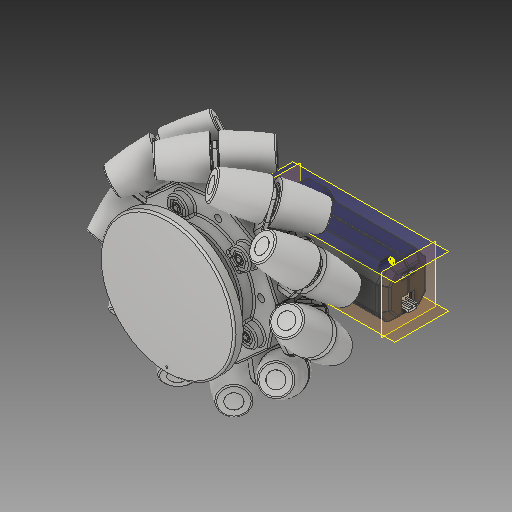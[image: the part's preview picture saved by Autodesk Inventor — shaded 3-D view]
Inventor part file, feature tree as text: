
AUTODESK INVENTOR PART (.ipt)
format: ipt  version: 2019 (Build 230136000, 136)  size: 17,353,216 bytes
history: native  units: in
note: dims shown in document units (in); Inventor stores cm internally (conversion verified against a paired STEP export)
features: other x108, plane x4
ambient origin geometry x8: Origin, YZ Plane, XZ Plane, XY Plane, X Axis, Y Axis, Z Axis, Center Point
bodies: Solid1 (feature_tree)
feature tree (112):
  other  "Wheel Sub-Assembly.iam"
  other  "wheel hubcap.ipt:1"
  other  "6inchMecanumLeft217-2799.20121203.iam:1::217-2799-001 Rev1.ipt:1"
  other  "6inchMecanumLeft217-2799.20121203.iam:1::217-2799-001 Rev1.ipt:2"
  other  "6inchMecanumLeft217-2799.20121203.iam:1::217-2799-002 Rev1.ipt:1"
  other  "6inchMecanumLeft217-2799.20121203.iam:1::217-2586-003 Rev2.ipt:1"
  other  "6inchMecanumLeft217-2799.20121203.iam:1::217-2586-003 Rev2.ipt:2"
  other  "6inchMecanumLeft217-2799.20121203.iam:1::217-2586-004 Rev1.ipt:1"
  other  "6inchMecanumLeft217-2799.20121203.iam:1::217-2586-004 Rev1.ipt:2"
  other  "6inchMecanumLeft217-2799.20121203.iam:1::217-2586-007 Rev1.ipt:1"
  other  "6inchMecanumLeft217-2799.20121203.iam:1::217-2586-008 Rev1.ipt:1"
  other  "6inchMecanumLeft217-2799.20121203.iam:1::NUT-832-NYLOCK.ipt:1"
  other  "6inchMecanumLeft217-2799.20121203.iam:1::SCREW-832-1250.ipt:1"
  other  "6inchMecanumLeft217-2799.20121203.iam:1::217-2586-007 Rev1.ipt:2"
  other  "6inchMecanumLeft217-2799.20121203.iam:1::217-2586-007 Rev1.ipt:3"
  other  "6inchMecanumLeft217-2799.20121203.iam:1::217-2586-007 Rev1.ipt:4"
  other  "6inchMecanumLeft217-2799.20121203.iam:1::217-2586-007 Rev1.ipt:5"
  other  "6inchMecanumLeft217-2799.20121203.iam:1::217-2586-007 Rev1.ipt:6"
  other  "6inchMecanumLeft217-2799.20121203.iam:1::217-2586-007 Rev1.ipt:7"
  other  "6inchMecanumLeft217-2799.20121203.iam:1::217-2586-007 Rev1.ipt:8"
  other  "6inchMecanumLeft217-2799.20121203.iam:1::217-2586-007 Rev1.ipt:9"
  other  "6inchMecanumLeft217-2799.20121203.iam:1::217-2586-007 Rev1.ipt:10"
  other  "6inchMecanumLeft217-2799.20121203.iam:1::217-2586-004 Rev1.ipt:3"
  other  "6inchMecanumLeft217-2799.20121203.iam:1::217-2586-004 Rev1.ipt:4"
  other  "6inchMecanumLeft217-2799.20121203.iam:1::217-2586-004 Rev1.ipt:5"
  other  "6inchMecanumLeft217-2799.20121203.iam:1::217-2586-004 Rev1.ipt:6"
  other  "6inchMecanumLeft217-2799.20121203.iam:1::217-2586-004 Rev1.ipt:7"
  other  "6inchMecanumLeft217-2799.20121203.iam:1::217-2586-004 Rev1.ipt:8"
  other  "6inchMecanumLeft217-2799.20121203.iam:1::217-2586-004 Rev1.ipt:9"
  other  "6inchMecanumLeft217-2799.20121203.iam:1::217-2586-004 Rev1.ipt:10"
  other  "6inchMecanumLeft217-2799.20121203.iam:1::217-2586-004 Rev1.ipt:11"
  other  "6inchMecanumLeft217-2799.20121203.iam:1::217-2586-004 Rev1.ipt:12"
  other  "6inchMecanumLeft217-2799.20121203.iam:1::217-2586-004 Rev1.ipt:13"
  other  "6inchMecanumLeft217-2799.20121203.iam:1::217-2586-004 Rev1.ipt:14"
  other  "6inchMecanumLeft217-2799.20121203.iam:1::217-2586-004 Rev1.ipt:15"
  other  "6inchMecanumLeft217-2799.20121203.iam:1::217-2586-004 Rev1.ipt:16"
  other  "6inchMecanumLeft217-2799.20121203.iam:1::217-2586-004 Rev1.ipt:17"
  other  "6inchMecanumLeft217-2799.20121203.iam:1::217-2586-004 Rev1.ipt:18"
  other  "6inchMecanumLeft217-2799.20121203.iam:1::217-2586-004 Rev1.ipt:19"
  other  "6inchMecanumLeft217-2799.20121203.iam:1::217-2586-004 Rev1.ipt:20"
  other  "6inchMecanumLeft217-2799.20121203.iam:1::217-2586-003 Rev2.ipt:3"
  other  "6inchMecanumLeft217-2799.20121203.iam:1::217-2586-003 Rev2.ipt:4"
  other  "6inchMecanumLeft217-2799.20121203.iam:1::217-2586-003 Rev2.ipt:5"
  other  "6inchMecanumLeft217-2799.20121203.iam:1::217-2586-003 Rev2.ipt:6"
  other  "6inchMecanumLeft217-2799.20121203.iam:1::217-2586-003 Rev2.ipt:7"
  other  "6inchMecanumLeft217-2799.20121203.iam:1::217-2586-003 Rev2.ipt:8"
  other  "6inchMecanumLeft217-2799.20121203.iam:1::217-2586-003 Rev2.ipt:9"
  other  "6inchMecanumLeft217-2799.20121203.iam:1::217-2586-003 Rev2.ipt:10"
  other  "6inchMecanumLeft217-2799.20121203.iam:1::217-2586-003 Rev2.ipt:11"
  other  "6inchMecanumLeft217-2799.20121203.iam:1::217-2586-003 Rev2.ipt:12"
  other  "6inchMecanumLeft217-2799.20121203.iam:1::217-2586-003 Rev2.ipt:13"
  other  "6inchMecanumLeft217-2799.20121203.iam:1::217-2586-003 Rev2.ipt:14"
  other  "6inchMecanumLeft217-2799.20121203.iam:1::217-2586-003 Rev2.ipt:15"
  other  "6inchMecanumLeft217-2799.20121203.iam:1::217-2586-003 Rev2.ipt:16"
  other  "6inchMecanumLeft217-2799.20121203.iam:1::217-2586-003 Rev2.ipt:17"
  other  "6inchMecanumLeft217-2799.20121203.iam:1::217-2586-003 Rev2.ipt:18"
  other  "6inchMecanumLeft217-2799.20121203.iam:1::217-2586-003 Rev2.ipt:19"
  other  "6inchMecanumLeft217-2799.20121203.iam:1::217-2586-003 Rev2.ipt:20"
  other  "6inchMecanumLeft217-2799.20121203.iam:1::217-2799-002 Rev1.ipt:2"
  other  "6inchMecanumLeft217-2799.20121203.iam:1::217-2799-002 Rev1.ipt:3"
  other  "6inchMecanumLeft217-2799.20121203.iam:1::217-2799-002 Rev1.ipt:4"
  other  "6inchMecanumLeft217-2799.20121203.iam:1::217-2799-002 Rev1.ipt:5"
  other  "6inchMecanumLeft217-2799.20121203.iam:1::217-2799-002 Rev1.ipt:6"
  other  "6inchMecanumLeft217-2799.20121203.iam:1::217-2799-002 Rev1.ipt:7"
  other  "6inchMecanumLeft217-2799.20121203.iam:1::217-2799-002 Rev1.ipt:8"
  other  "6inchMecanumLeft217-2799.20121203.iam:1::217-2799-002 Rev1.ipt:9"
  other  "6inchMecanumLeft217-2799.20121203.iam:1::217-2799-002 Rev1.ipt:10"
  other  "6inchMecanumLeft217-2799.20121203.iam:1::217-2586-008 Rev1.ipt:2"
  other  "6inchMecanumLeft217-2799.20121203.iam:1::217-2586-008 Rev1.ipt:3"
  other  "6inchMecanumLeft217-2799.20121203.iam:1::217-2586-008 Rev1.ipt:4"
  other  "6inchMecanumLeft217-2799.20121203.iam:1::217-2586-008 Rev1.ipt:5"
  other  "6inchMecanumLeft217-2799.20121203.iam:1::217-2586-008 Rev1.ipt:6"
  other  "6inchMecanumLeft217-2799.20121203.iam:1::SCREW-832-1250.ipt:2"
  other  "6inchMecanumLeft217-2799.20121203.iam:1::SCREW-832-1250.ipt:3"
  other  "6inchMecanumLeft217-2799.20121203.iam:1::SCREW-832-1250.ipt:4"
  other  "6inchMecanumLeft217-2799.20121203.iam:1::SCREW-832-1250.ipt:5"
  other  "6inchMecanumLeft217-2799.20121203.iam:1::NUT-832-NYLOCK.ipt:2"
  other  "6inchMecanumLeft217-2799.20121203.iam:1::NUT-832-NYLOCK.ipt:3"
  other  "6inchMecanumLeft217-2799.20121203.iam:1::NUT-832-NYLOCK.ipt:4"
  other  "6inchMecanumLeft217-2799.20121203.iam:1::NUT-832-NYLOCK.ipt:5"
  other  "6inchMecanumLeft217-2799.20121203.iam:1::217-2586-005 Rev2.ipt:1"
  other  "6inchMecanumLeft217-2799.20121203.iam:1::217-2586-005 Rev2.ipt:2"
  other  "6inchMecanumLeft217-2799.20121203.iam:1::217-2586-005 Rev2.ipt:3"
  other  "6inchMecanumLeft217-2799.20121203.iam:1::217-2586-005 Rev2.ipt:4"
  other  "6inchMecanumLeft217-2799.20121203.iam:1::217-2586-005 Rev2.ipt:5"
  other  "6inchMecanumLeft217-2799.20121203.iam:1::217-2586-005 Rev2.ipt:6"
  other  "6inchMecanumLeft217-2799.20121203.iam:1::217-2586-005 Rev2.ipt:7"
  other  "6inchMecanumLeft217-2799.20121203.iam:1::217-2586-005 Rev2.ipt:8"
  other  "6inchMecanumLeft217-2799.20121203.iam:1::217-2586-005 Rev2.ipt:9"
  other  "6inchMecanumLeft217-2799.20121203.iam:1::217-2586-005 Rev2.ipt:10"
  other  "6inchMecanumLeft217-2799.20121203.iam:1::217-2586-005 Rev2.ipt:11"
  other  "6inchMecanumLeft217-2799.20121203.iam:1::217-2586-005 Rev2.ipt:12"
  other  "6inchMecanumLeft217-2799.20121203.iam:1::217-2586-005 Rev2.ipt:13"
  other  "6inchMecanumLeft217-2799.20121203.iam:1::217-2586-005 Rev2.ipt:14"
  other  "6inchMecanumLeft217-2799.20121203.iam:1::217-2586-005 Rev2.ipt:15"
  other  "6inchMecanumLeft217-2799.20121203.iam:1::217-2586-005 Rev2.ipt:16"
  other  "6inchMecanumLeft217-2799.20121203.iam:1::217-2586-005 Rev2.ipt:17"
  other  "6inchMecanumLeft217-2799.20121203.iam:1::217-2586-005 Rev2.ipt:18"
  other  "6inchMecanumLeft217-2799.20121203.iam:1::217-2586-005 Rev2.ipt:19"
  other  "6inchMecanumLeft217-2799.20121203.iam:1::217-2586-005 Rev2.ipt:20"
  other  "REV-41-1300HexMotor.ipt:1"
  other  "REV-41-1349HexAxle.ipt:1"
  other  "VersaHub 500 Hex.ipt:1"
  other  "545690 assembly.ipt:1"
  other  "Wheel Sub-Assembly.iam_Bodies"
  plane  "Work Plane1"
  plane  "Work Plane2"
  plane  "Work Plane3"
  plane  "Work Plane4"
  other  "Srf1"
  other  "Work Axis1"
  other  "Srf1::Derived"
